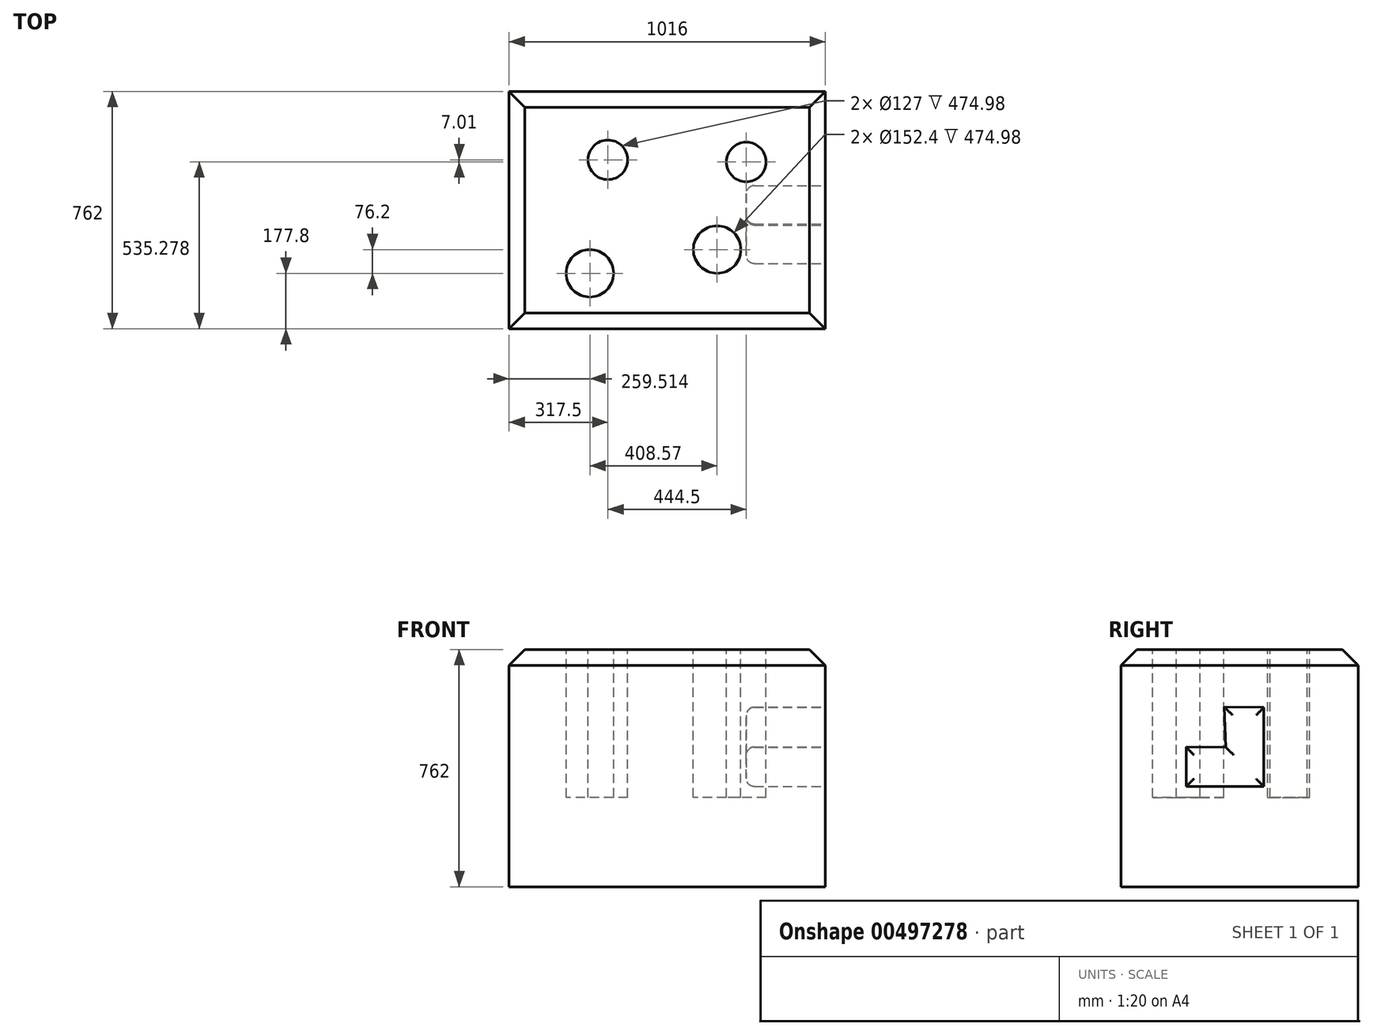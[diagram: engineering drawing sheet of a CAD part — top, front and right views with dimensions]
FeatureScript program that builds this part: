
annotation { "Feature Type Name" : "Feature", "Feature Type Description" : "" }
export const myFeature = defineFeature(function(context is Context, id is Id, definition is map)
    precondition{}
    {
        {
            var Q0;
            Q0=qCreatedBy(makeId("Top.planeOp"),FACE);
            var sketch = newSketch(context, id + "F0", { "sketchPlane" : qUnion([Q0])});
            skLineSegment(sketch, "E0.bottom", {"start": v(508, -381) * mm, "end": v(-508, -381) * mm});
            skLineSegment(sketch, "E0.top", {"start": v(508, 381) * mm, "end": v(-508, 381) * mm});
            skLineSegment(sketch, "E0.left", {"start": v(508, -381) * mm, "end": v(508, 381) * mm});
            skLineSegment(sketch, "E0.right", {"start": v(-508, -381) * mm, "end": v(-508, 381) * mm});
            skPoint(sketch, "E0.middle", {"position": v(0, 0) * mm});
            skSolve(sketch);
        }
        {
            var Q0;
            Q0 = qSketchRegion(id + "F0", true);
            extrude(context, id + "F1", {"entities" : qUnion([Q0]), "depth" : 762 * mm});
        }
        {
            var Q0;
            Q0=makeQuery(id+"F1.opExtrude","CAP_EDGE",EDGE,{"disambiguationData":[OSD([sQuery(id+"F0.wireOp",EDGE,"E0.bottom")])],"isStart":false});
            var Q1;
            Q1=makeQuery(id+"F1.opExtrude","CAP_EDGE",EDGE,{"disambiguationData":[OSD([sQuery(id+"F0.wireOp",EDGE,"E0.left")])],"isStart":false});
            var Q2;
            Q2=makeQuery(id+"F1.opExtrude","CAP_EDGE",EDGE,{"disambiguationData":[OSD([sQuery(id+"F0.wireOp",EDGE,"E0.top")])],"isStart":false});
            var Q3;
            Q3=makeQuery(id+"F1.opExtrude","CAP_FACE",FACE,{"disambiguationData":[OSD([sQuery(id+"F0.wireOp",EDGE,"E0.bottom"),sQuery(id+"F0.wireOp",EDGE,"E0.top"),sQuery(id+"F0.wireOp",EDGE,"E0.left"),sQuery(id+"F0.wireOp",EDGE,"E0.right")])],"isStart":false});
            chamfer(context, id + "F2", {"entities" : qUnion([Q0, Q1, Q2, Q3]), "width" : 50.8 * mm, "tangentPropagation" : true});
        }
        {
            var Q0;
            Q0=makeQuery(id+"F1.opExtrude","CAP_FACE",FACE,{"disambiguationData":[OSD([sQuery(id+"F0.wireOp",EDGE,"E0.bottom"),sQuery(id+"F0.wireOp",EDGE,"E0.top"),sQuery(id+"F0.wireOp",EDGE,"E0.left"),sQuery(id+"F0.wireOp",EDGE,"E0.right")])],"isStart":false});
            var sketch = newSketch(context, id + "F3", { "sketchPlane" : qUnion([Q0])});
            skCircle(sketch, "E1", {"center": v(-190.5, 161.29) * mm, "radius": 63.5 * mm});
            skCircle(sketch, "E2", {"center": v(254, 154.28) * mm, "radius": 63.5 * mm});
            skCircle(sketch, "E3", {"center": v(-248.49, -203.2) * mm, "radius": 76.2 * mm});
            skCircle(sketch, "E4", {"center": v(160.08, -127) * mm, "radius": 76.2 * mm});
            skSolve(sketch);
        }
        {
            var Q0;
            Q0=makeQuery(id+"F3.imprint","IMPRINT",FACE,{"disambiguationData":[TD([[makeQuery(id+"F3.imprint","IMPRINT",EDGE,{"derivedFrom":sQuery(id+"F3.wireOp",EDGE,"E2")}),1.0]])]});
            var Q1;
            Q1=makeQuery(id+"F3.imprint","IMPRINT",FACE,{"disambiguationData":[TD([[makeQuery(id+"F3.imprint","IMPRINT",EDGE,{"derivedFrom":sQuery(id+"F3.wireOp",EDGE,"E4")}),1.0]])]});
            var Q2;
            Q2=makeQuery(id+"F3.imprint","IMPRINT",FACE,{"disambiguationData":[TD([[makeQuery(id+"F3.imprint","IMPRINT",EDGE,{"derivedFrom":sQuery(id+"F3.wireOp",EDGE,"E1")}),1.0]])]});
            var Q3;
            Q3=makeQuery(id+"F3.imprint","IMPRINT",FACE,{"disambiguationData":[TD([[makeQuery(id+"F3.imprint","IMPRINT",EDGE,{"derivedFrom":sQuery(id+"F3.wireOp",EDGE,"E3")}),1.0]])]});
            extrude(context, id + "F4", {"entities" : qUnion([Q0, Q1, Q2, Q3]), "operationType" : NewBodyOperationType.REMOVE, "oppositeDirection" : true, "depth" : 474.98 * mm});
        }
        {
            var Q0;
            Q0=makeQuery(id+"F1.opExtrude","SWEPT_FACE",FACE,{"disambiguationData":[OSD([sQuery(id+"F0.wireOp",EDGE,"E0.left")])]});
            var sketch = newSketch(context, id + "F5", { "sketchPlane" : qUnion([Q0])});
            skLineSegment(sketch, "E5", {"start": v(-172.04, 321.88) * mm, "end": v(-172.04, 448.88) * mm});
            skLineSegment(sketch, "E6", {"start": v(-172.04, 448.88) * mm, "end": v(-45.04, 448.44) * mm});
            skLineSegment(sketch, "E7", {"start": v(-45.04, 448.44) * mm, "end": v(-48.83, 576.8) * mm});
            skLineSegment(sketch, "E8", {"start": v(-48.83, 576.8) * mm, "end": v(78.17, 575.88) * mm});
            skLineSegment(sketch, "E9", {"start": v(78.17, 575.88) * mm, "end": v(78.17, 321.88) * mm});
            skLineSegment(sketch, "E10", {"start": v(78.17, 321.88) * mm, "end": v(-172.04, 321.88) * mm});
            skSolve(sketch);
        }
        {
            var Q0;
            Q0 = qSketchRegion(id + "F5", true);
            extrude(context, id + "F6", {"entities" : qUnion([Q0]), "operationType" : NewBodyOperationType.REMOVE, "oppositeDirection" : true, "depth" : 254 * mm});
        }
        {
            var Q0;
            Q0=makeQuery(id+"F6.boolean.opBoolean","COPY",EDGE,{"derivedFrom":makeQuery(id+"F6.opExtrude","CAP_EDGE",EDGE,{"disambiguationData":[OSD([sQuery(id+"F5.wireOp",EDGE,"E6")])],"isStart":false})});
            var Q1;
            Q1=makeQuery(id+"F6.boolean.opBoolean","COPY",EDGE,{"derivedFrom":makeQuery(id+"F6.opExtrude","CAP_EDGE",EDGE,{"disambiguationData":[OSD([sQuery(id+"F5.wireOp",EDGE,"E7")])],"isStart":false})});
            var Q2;
            Q2=makeQuery(id+"F6.boolean.opBoolean","COPY",EDGE,{"derivedFrom":makeQuery(id+"F6.opExtrude","CAP_EDGE",EDGE,{"disambiguationData":[OSD([sQuery(id+"F5.wireOp",EDGE,"E8")])],"isStart":false})});
            var Q3;
            Q3=makeQuery(id+"F6.boolean.opBoolean","COPY",EDGE,{"derivedFrom":makeQuery(id+"F6.opExtrude","CAP_EDGE",EDGE,{"disambiguationData":[OSD([sQuery(id+"F5.wireOp",EDGE,"E9")])],"isStart":false})});
            var Q4;
            Q4=makeQuery(id+"F6.boolean.opBoolean","COPY",EDGE,{"derivedFrom":makeQuery(id+"F6.opExtrude","CAP_EDGE",EDGE,{"disambiguationData":[OSD([sQuery(id+"F5.wireOp",EDGE,"E10")])],"isStart":false})});
            var Q5;
            Q5=makeQuery(id+"F6.boolean.opBoolean","COPY",EDGE,{"derivedFrom":makeQuery(id+"F6.opExtrude","CAP_EDGE",EDGE,{"disambiguationData":[OSD([sQuery(id+"F5.wireOp",EDGE,"E5")])],"isStart":false})});
            fillet(context, id + "F7", {"entities" : qUnion([Q0, Q1, Q2, Q3, Q4, Q5]), "radius" : 25.4 * mm, "tangentPropagation" : true, "allowEdgeOverflow" : false});
        }
    });
